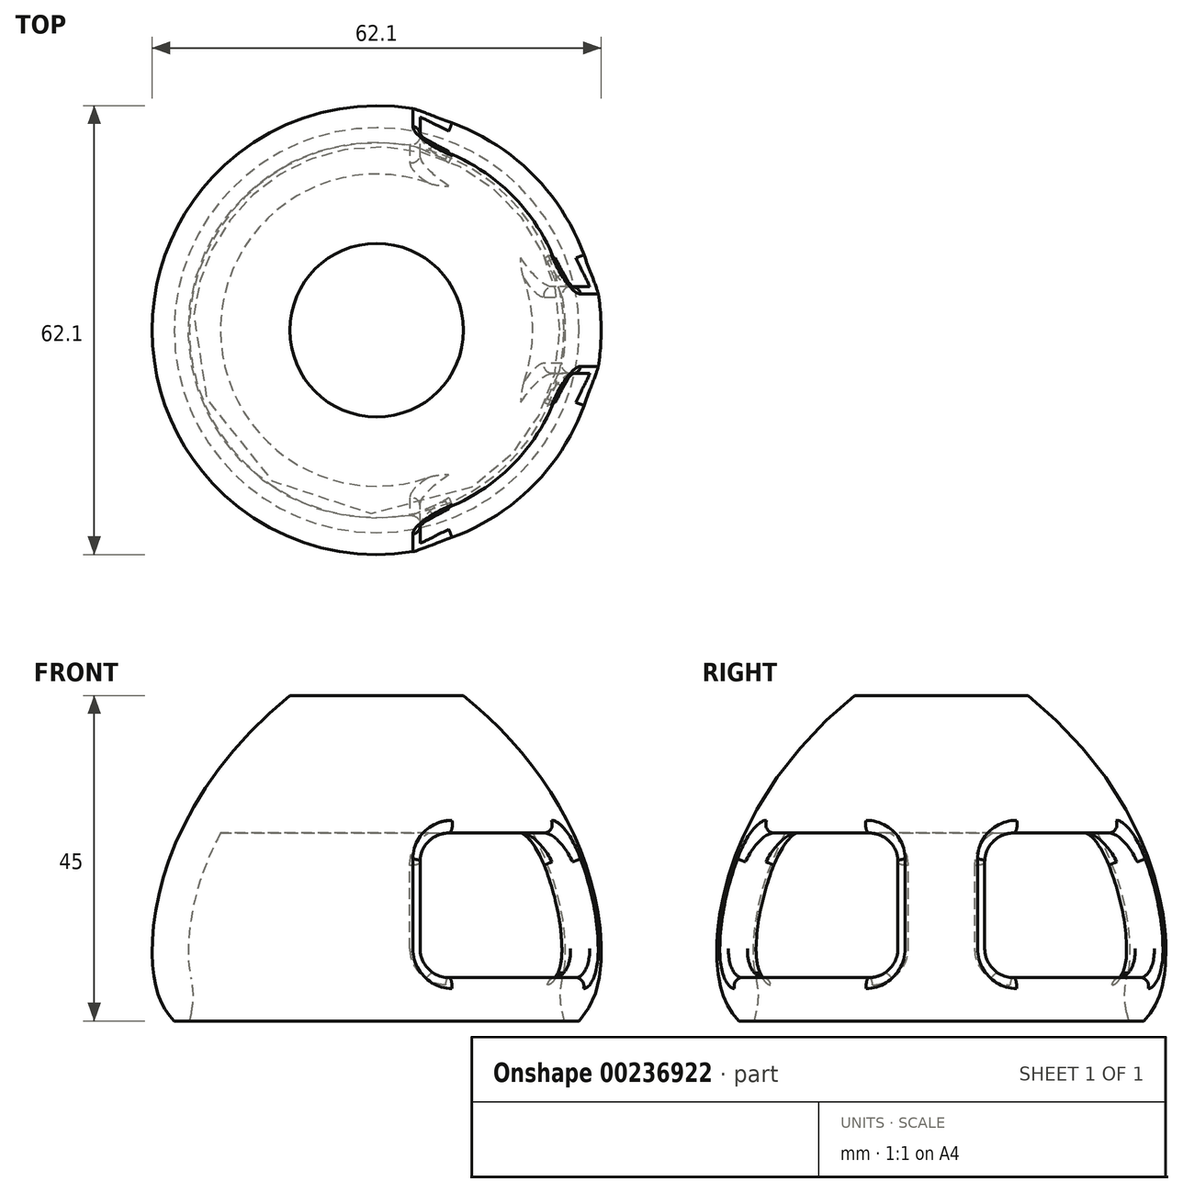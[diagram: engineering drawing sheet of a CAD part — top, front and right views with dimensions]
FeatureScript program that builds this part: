
annotation { "Feature Type Name" : "Feature", "Feature Type Description" : "" }
export const myFeature = defineFeature(function(context is Context, id is Id, definition is map)
    precondition{}
    {
        {
            var Q0;
            Q0=qCreatedBy(makeId("Front.planeOp"),FACE);
            var sketch = newSketch(context, id + "F0", { "sketchPlane" : qUnion([Q0])});
            skLineSegment(sketch, "E0", {"start": v(0, 0) * mm, "end": v(0, 45) * mm});
            skLineSegment(sketch, "E1", {"start": v(0, 45) * mm, "end": v(12, 45) * mm});
            skLineSegment(sketch, "E2", {"start": v(0, 0) * mm, "end": v(28, 0) * mm});
            skLineSegment(sketch, "E3", {"start": v(28, 0) * mm, "end": v(28, 8) * mm, "construction": true});
            skLineSegment(sketch, "E4", {"start": v(28, 8) * mm, "end": v(31, 8) * mm, "construction": true});
            skFitSpline(sketch, "E5", {"points": [v(12, 45) * mm, v(31, 8) * mm, v(28, 0) * mm], "startDerivative": vector(69.76, -56.68) * mm, "endDerivative": vector(-16.2, -16.73) * mm});
            skSolve(sketch);
        }
        {
            var Q0;
            Q0 = qSketchRegion(id + "F0", true);
            var Q1;
            Q1=sQuery(id+"F0.wireOp",EDGE,"E0");
            revolve(context, id + "F1", {"entities" : qUnion([Q0]), "axis" : qUnion([Q1]), "revolveType" : RevolveType.FULL});
        }
        {
            var Q0;
            Q0=makeQuery(id+"F1.opRevolve","SWEPT_FACE",FACE,{"disambiguationData":[OSD([sQuery(id+"F0.wireOp",EDGE,"E2")])]});
            shell(context, id + "F2", {"entities" : qUnion([Q0]), "thickness" : 5 * mm});
        }
        {
            var Q0;
            Q0=qCreatedBy(makeId("Top.planeOp"),FACE);
            cPlane(context, id + "F3", {"entities" : qUnion([Q0]), "cplaneType" : CPlaneType.OFFSET, "offset" : 26 * mm, "width" : 150 * mm, "height" : 150 * mm});
        }
        {
            var Q0;
            Q0=qCreatedBy(id+"F3.planeOp",FACE);
            var sketch = newSketch(context, id + "F4", { "sketchPlane" : qUnion([Q0])});
            skCircle(sketch, "E6", {"center": v(0, 0) * mm, "radius": 27.24 * mm});
            skSolve(sketch);
        }
        {
            var Q0;
            Q0 = qSketchRegion(id + "F4", true);
            var Q1;
            Q1=makeQuery(id+"F1.opRevolve","SWEPT_BODY",BODY,{"disambiguationData":[OSD([sQuery(id+"F0.wireOp",EDGE,"E0"),sQuery(id+"F0.wireOp",EDGE,"E1"),sQuery(id+"F0.wireOp",EDGE,"E2"),sQuery(id+"F0.wireOp",EDGE,"E5")])]});
            extrude(context, id + "F5", {"entities" : qUnion([Q0]), "operationType" : NewBodyOperationType.ADD, "endBound" : BoundingType.UP_TO_BODY, "endBoundEntityBody" : qUnion([Q1]), "depth" : 25 * mm});
        }
        {
            var Q0;
            Q0=makeQuery(id+"F2.opShell","OFFSET_EDGE",EDGE,{"disambiguationData":[OSD([sQuery(id+"F0.wireOp",EDGE,"E2"),sQuery(id+"F0.wireOp",EDGE,"E5")])]});
            chamfer(context, id + "F6", {"entities" : qUnion([Q0]), "chamferType" : ChamferType.TWO_OFFSETS, "width1" : 6 * mm, "oppositeDirection" : false, "width2" : 5 * mm, "tangentPropagation" : true});
        }
        {
            var Q0;
            {var subQ0=sQuery(id+"F0.wireOp",EDGE,"E5");Q0=makeQuery(id+"F6.opChamfer","BLEND_EDGE",EDGE,{"blendedFrom":[makeQuery(id+"F2.opShell","OFFSET_EDGE",EDGE,{"disambiguationData":[OSD([sQuery(id+"F0.wireOp",EDGE,"E2"),subQ0])]}),makeQuery(id+"F2.opShell","OFFSET_FACE",FACE,{"disambiguationData":[OSD([subQ0])]})],"blendedInto":[makeQuery(id+"F2.opShell","OFFSET_FACE",FACE,{"disambiguationData":[OSD([subQ0])]})]});}
            fillet(context, id + "F7", {"entities" : qUnion([Q0]), "radius" : 10 * mm, "tangentPropagation" : true, "allowEdgeOverflow" : false});
        }
        {
            var Q0;
            Q0=qCreatedBy(makeId("Top.planeOp"),FACE);
            cPlane(context, id + "F8", {"entities" : qUnion([Q0]), "cplaneType" : CPlaneType.OFFSET, "offset" : 6 * mm, "width" : 150 * mm, "height" : 150 * mm});
        }
        {
            var Q0;
            Q0=qCreatedBy(id+"F8.planeOp",FACE);
            var sketch = newSketch(context, id + "F9", { "sketchPlane" : qUnion([Q0])});
            skLineSegment(sketch, "E7.bottom", {"start": v(6, -44.78) * mm, "end": v(-6, -44.78) * mm});
            skLineSegment(sketch, "E7.top", {"start": v(6, 44.78) * mm, "end": v(-6, 44.78) * mm});
            skLineSegment(sketch, "E7.left", {"start": v(6, -44.78) * mm, "end": v(6, 44.78) * mm});
            skLineSegment(sketch, "E7.right", {"start": v(-6, -44.78) * mm, "end": v(-6, 44.78) * mm});
            skPoint(sketch, "E7.middle", {"position": v(0, 0) * mm});
            skLineSegment(sketch, "E8.bottom", {"start": v(39.59, 6) * mm, "end": v(-39.59, 6) * mm});
            skLineSegment(sketch, "E8.top", {"start": v(39.59, -6) * mm, "end": v(-39.59, -6) * mm});
            skLineSegment(sketch, "E8.left", {"start": v(39.59, 6) * mm, "end": v(39.59, -6) * mm});
            skLineSegment(sketch, "E8.right", {"start": v(-39.59, 6) * mm, "end": v(-39.59, -6) * mm});
            skCircle(sketch, "E9", {"center": v(0, 0) * mm, "radius": 40.04 * mm});
            skSolve(sketch);
        }
        {
            var Q0;
            {var subQ0=sQuery(id+"F9.wireOp",EDGE,"E9");var subQ1=sQuery(id+"F9.wireOp",EDGE,"E7.right");var subQ2=makeQuery(id+"F9.imprint","INTERSECT",VERTEX,{"disambiguationData":[OD(0.0)],"derivedFrom":[subQ1,subQ0]});Q0=makeQuery(id+"F9.imprint","IMPRINT",FACE,{"disambiguationData":[TD([[makeQuery(id+"F9.imprint","IMPRINT",EDGE,{"disambiguationData":[TD([[subQ2,-1.0]])],"derivedFrom":subQ1}),1.0]])]});}
            var Q1;
            {var subQ0=sQuery(id+"F9.wireOp",EDGE,"E9");var subQ1=sQuery(id+"F9.wireOp",EDGE,"E7.left");var subQ2=makeQuery(id+"F9.imprint","INTERSECT",VERTEX,{"disambiguationData":[OD(0.0)],"derivedFrom":[subQ1,subQ0]});Q1=makeQuery(id+"F9.imprint","IMPRINT",FACE,{"disambiguationData":[TD([[makeQuery(id+"F9.imprint","IMPRINT",EDGE,{"disambiguationData":[TD([[subQ2,-1.0]])],"derivedFrom":subQ1}),-1.0]])]});}
            var Q2;
            {var subQ0=sQuery(id+"F9.wireOp",EDGE,"E9");var subQ1=sQuery(id+"F9.wireOp",EDGE,"E7.right");var subQ2=makeQuery(id+"F9.imprint","INTERSECT",VERTEX,{"disambiguationData":[OD(1.0)],"derivedFrom":[subQ1,subQ0]});Q2=makeQuery(id+"F9.imprint","IMPRINT",FACE,{"disambiguationData":[TD([[makeQuery(id+"F9.imprint","IMPRINT",EDGE,{"disambiguationData":[TD([[subQ2,1.0]])],"derivedFrom":subQ1}),1.0]])]});}
            var Q3;
            {var subQ0=sQuery(id+"F9.wireOp",EDGE,"E9");var subQ1=sQuery(id+"F9.wireOp",EDGE,"E7.left");var subQ2=makeQuery(id+"F9.imprint","INTERSECT",VERTEX,{"disambiguationData":[OD(1.0)],"derivedFrom":[subQ1,subQ0]});Q3=makeQuery(id+"F9.imprint","IMPRINT",FACE,{"disambiguationData":[TD([[makeQuery(id+"F9.imprint","IMPRINT",EDGE,{"disambiguationData":[TD([[subQ2,1.0]])],"derivedFrom":subQ1}),-1.0]])]});}
            var Q4;
            Q4=makeQuery(id+"F5.opExtrude","CAP_FACE",FACE,{"disambiguationData":[OSD([sQuery(id+"F4.wireOp",EDGE,"E6")])],"isStart":true});
            extrude(context, id + "F10", {"entities" : qUnion([Q0, Q1, Q2, Q3]), "operationType" : NewBodyOperationType.REMOVE, "endBound" : BoundingType.UP_TO_SURFACE, "endBoundEntityFace" : qUnion([Q4]), "depth" : 25 * mm});
        }
        {
            var Q0;
            {var subQ0=sQuery(id+"F9.wireOp",EDGE,"E7.right");Q0=makeQuery(id+"F10.boolean.opBoolean","COPY",EDGE,{"derivedFrom":makeQuery(id+"F10.opExtrude","CAP_EDGE",EDGE,{"disambiguationData":[OSD([subQ0]),TDD([makeQuery(id+"F9.imprint","IMPRINT",EDGE,{"disambiguationData":[TD([[makeQuery(id+"F9.imprint","INTERSECT",VERTEX,{"disambiguationData":[OD(0.0)],"derivedFrom":[subQ0,sQuery(id+"F9.wireOp",EDGE,"E9")]}),-1.0]])],"derivedFrom":subQ0})])],"isStart":true})});}
            var Q1;
            {var subQ0=sQuery(id+"F9.wireOp",EDGE,"E7.right");Q1=makeQuery(id+"F10.boolean.opBoolean","COPY",EDGE,{"derivedFrom":makeQuery(id+"F10.opExtrude","CAP_EDGE",EDGE,{"disambiguationData":[OSD([subQ0]),TDD([makeQuery(id+"F9.imprint","IMPRINT",EDGE,{"disambiguationData":[TD([[makeQuery(id+"F9.imprint","INTERSECT",VERTEX,{"disambiguationData":[OD(0.0)],"derivedFrom":[subQ0,sQuery(id+"F9.wireOp",EDGE,"E9")]}),-1.0]])],"derivedFrom":subQ0})])],"isStart":false})});}
            var Q2;
            {var subQ0=sQuery(id+"F9.wireOp",EDGE,"E8.top");Q2=makeQuery(id+"F10.boolean.opBoolean","COPY",EDGE,{"derivedFrom":makeQuery(id+"F10.opExtrude","CAP_EDGE",EDGE,{"disambiguationData":[OSD([subQ0]),TDD([makeQuery(id+"F9.imprint","IMPRINT",EDGE,{"disambiguationData":[TD([[makeQuery(id+"F9.imprint","INTERSECT",VERTEX,{"derivedFrom":[sQuery(id+"F9.wireOp",EDGE,"E7.right"),subQ0]}),-1.0]])],"derivedFrom":subQ0})])],"isStart":false})});}
            var Q3;
            {var subQ0=sQuery(id+"F9.wireOp",EDGE,"E8.top");Q3=makeQuery(id+"F10.boolean.opBoolean","COPY",EDGE,{"derivedFrom":makeQuery(id+"F10.opExtrude","CAP_EDGE",EDGE,{"disambiguationData":[OSD([subQ0]),TDD([makeQuery(id+"F9.imprint","IMPRINT",EDGE,{"disambiguationData":[TD([[makeQuery(id+"F9.imprint","INTERSECT",VERTEX,{"derivedFrom":[sQuery(id+"F9.wireOp",EDGE,"E7.right"),subQ0]}),-1.0]])],"derivedFrom":subQ0})])],"isStart":true})});}
            var Q4;
            {var subQ0=sQuery(id+"F9.wireOp",EDGE,"E8.bottom");Q4=makeQuery(id+"F10.boolean.opBoolean","COPY",EDGE,{"derivedFrom":makeQuery(id+"F10.opExtrude","CAP_EDGE",EDGE,{"disambiguationData":[OSD([subQ0]),TDD([makeQuery(id+"F9.imprint","IMPRINT",EDGE,{"disambiguationData":[TD([[makeQuery(id+"F9.imprint","INTERSECT",VERTEX,{"derivedFrom":[sQuery(id+"F9.wireOp",EDGE,"E7.right"),subQ0]}),-1.0]])],"derivedFrom":subQ0})])],"isStart":true})});}
            var Q5;
            {var subQ0=sQuery(id+"F9.wireOp",EDGE,"E8.bottom");Q5=makeQuery(id+"F10.boolean.opBoolean","COPY",EDGE,{"derivedFrom":makeQuery(id+"F10.opExtrude","CAP_EDGE",EDGE,{"disambiguationData":[OSD([subQ0]),TDD([makeQuery(id+"F9.imprint","IMPRINT",EDGE,{"disambiguationData":[TD([[makeQuery(id+"F9.imprint","INTERSECT",VERTEX,{"derivedFrom":[sQuery(id+"F9.wireOp",EDGE,"E7.right"),subQ0]}),-1.0]])],"derivedFrom":subQ0})])],"isStart":false})});}
            var Q6;
            {var subQ0=sQuery(id+"F9.wireOp",EDGE,"E7.right");Q6=makeQuery(id+"F10.boolean.opBoolean","COPY",EDGE,{"derivedFrom":makeQuery(id+"F10.opExtrude","CAP_EDGE",EDGE,{"disambiguationData":[OSD([subQ0]),TDD([makeQuery(id+"F9.imprint","IMPRINT",EDGE,{"disambiguationData":[TD([[makeQuery(id+"F9.imprint","INTERSECT",VERTEX,{"disambiguationData":[OD(1.0)],"derivedFrom":[subQ0,sQuery(id+"F9.wireOp",EDGE,"E9")]}),1.0]])],"derivedFrom":subQ0})])],"isStart":false})});}
            var Q7;
            {var subQ0=sQuery(id+"F9.wireOp",EDGE,"E7.right");Q7=makeQuery(id+"F10.boolean.opBoolean","COPY",EDGE,{"derivedFrom":makeQuery(id+"F10.opExtrude","CAP_EDGE",EDGE,{"disambiguationData":[OSD([subQ0]),TDD([makeQuery(id+"F9.imprint","IMPRINT",EDGE,{"disambiguationData":[TD([[makeQuery(id+"F9.imprint","INTERSECT",VERTEX,{"disambiguationData":[OD(1.0)],"derivedFrom":[subQ0,sQuery(id+"F9.wireOp",EDGE,"E9")]}),1.0]])],"derivedFrom":subQ0})])],"isStart":true})});}
            var Q8;
            {var subQ0=sQuery(id+"F9.wireOp",EDGE,"E7.left");Q8=makeQuery(id+"F10.boolean.opBoolean","COPY",EDGE,{"derivedFrom":makeQuery(id+"F10.opExtrude","CAP_EDGE",EDGE,{"disambiguationData":[OSD([subQ0]),TDD([makeQuery(id+"F9.imprint","IMPRINT",EDGE,{"disambiguationData":[TD([[makeQuery(id+"F9.imprint","INTERSECT",VERTEX,{"disambiguationData":[OD(1.0)],"derivedFrom":[subQ0,sQuery(id+"F9.wireOp",EDGE,"E9")]}),1.0]])],"derivedFrom":subQ0})])],"isStart":true})});}
            var Q9;
            {var subQ0=sQuery(id+"F9.wireOp",EDGE,"E7.left");Q9=makeQuery(id+"F10.boolean.opBoolean","COPY",EDGE,{"derivedFrom":makeQuery(id+"F10.opExtrude","CAP_EDGE",EDGE,{"disambiguationData":[OSD([subQ0]),TDD([makeQuery(id+"F9.imprint","IMPRINT",EDGE,{"disambiguationData":[TD([[makeQuery(id+"F9.imprint","INTERSECT",VERTEX,{"disambiguationData":[OD(1.0)],"derivedFrom":[subQ0,sQuery(id+"F9.wireOp",EDGE,"E9")]}),1.0]])],"derivedFrom":subQ0})])],"isStart":false})});}
            var Q10;
            {var subQ0=sQuery(id+"F9.wireOp",EDGE,"E8.bottom");Q10=makeQuery(id+"F10.boolean.opBoolean","COPY",EDGE,{"derivedFrom":makeQuery(id+"F10.opExtrude","CAP_EDGE",EDGE,{"disambiguationData":[OSD([subQ0]),TDD([makeQuery(id+"F9.imprint","IMPRINT",EDGE,{"disambiguationData":[TD([[makeQuery(id+"F9.imprint","INTERSECT",VERTEX,{"derivedFrom":[sQuery(id+"F9.wireOp",EDGE,"E7.left"),subQ0]}),1.0]])],"derivedFrom":subQ0})])],"isStart":false})});}
            var Q11;
            {var subQ0=sQuery(id+"F9.wireOp",EDGE,"E8.bottom");Q11=makeQuery(id+"F10.boolean.opBoolean","COPY",EDGE,{"derivedFrom":makeQuery(id+"F10.opExtrude","CAP_EDGE",EDGE,{"disambiguationData":[OSD([subQ0]),TDD([makeQuery(id+"F9.imprint","IMPRINT",EDGE,{"disambiguationData":[TD([[makeQuery(id+"F9.imprint","INTERSECT",VERTEX,{"derivedFrom":[sQuery(id+"F9.wireOp",EDGE,"E7.left"),subQ0]}),1.0]])],"derivedFrom":subQ0})])],"isStart":true})});}
            var Q12;
            {var subQ0=sQuery(id+"F9.wireOp",EDGE,"E8.top");Q12=makeQuery(id+"F10.boolean.opBoolean","COPY",EDGE,{"derivedFrom":makeQuery(id+"F10.opExtrude","CAP_EDGE",EDGE,{"disambiguationData":[OSD([subQ0]),TDD([makeQuery(id+"F9.imprint","IMPRINT",EDGE,{"disambiguationData":[TD([[makeQuery(id+"F9.imprint","INTERSECT",VERTEX,{"derivedFrom":[sQuery(id+"F9.wireOp",EDGE,"E7.left"),subQ0]}),1.0]])],"derivedFrom":subQ0})])],"isStart":true})});}
            var Q13;
            {var subQ0=sQuery(id+"F9.wireOp",EDGE,"E7.left");Q13=makeQuery(id+"F10.boolean.opBoolean","COPY",EDGE,{"derivedFrom":makeQuery(id+"F10.opExtrude","CAP_EDGE",EDGE,{"disambiguationData":[OSD([subQ0]),TDD([makeQuery(id+"F9.imprint","IMPRINT",EDGE,{"disambiguationData":[TD([[makeQuery(id+"F9.imprint","INTERSECT",VERTEX,{"disambiguationData":[OD(0.0)],"derivedFrom":[subQ0,sQuery(id+"F9.wireOp",EDGE,"E9")]}),-1.0]])],"derivedFrom":subQ0})])],"isStart":true})});}
            var Q14;
            {var subQ0=sQuery(id+"F9.wireOp",EDGE,"E7.left");Q14=makeQuery(id+"F10.boolean.opBoolean","COPY",EDGE,{"derivedFrom":makeQuery(id+"F10.opExtrude","CAP_EDGE",EDGE,{"disambiguationData":[OSD([subQ0]),TDD([makeQuery(id+"F9.imprint","IMPRINT",EDGE,{"disambiguationData":[TD([[makeQuery(id+"F9.imprint","INTERSECT",VERTEX,{"disambiguationData":[OD(0.0)],"derivedFrom":[subQ0,sQuery(id+"F9.wireOp",EDGE,"E9")]}),-1.0]])],"derivedFrom":subQ0})])],"isStart":false})});}
            var Q15;
            {var subQ0=sQuery(id+"F9.wireOp",EDGE,"E8.top");Q15=makeQuery(id+"F10.boolean.opBoolean","COPY",EDGE,{"derivedFrom":makeQuery(id+"F10.opExtrude","CAP_EDGE",EDGE,{"disambiguationData":[OSD([subQ0]),TDD([makeQuery(id+"F9.imprint","IMPRINT",EDGE,{"disambiguationData":[TD([[makeQuery(id+"F9.imprint","INTERSECT",VERTEX,{"derivedFrom":[sQuery(id+"F9.wireOp",EDGE,"E7.left"),subQ0]}),1.0]])],"derivedFrom":subQ0})])],"isStart":false})});}
            fillet(context, id + "F11", {"entities" : qUnion([Q0, Q1, Q2, Q3, Q4, Q5, Q6, Q7, Q8, Q9, Q10, Q11, Q12, Q13, Q14, Q15]), "radius" : 4 * mm, "tangentPropagation" : true, "allowEdgeOverflow" : false});
        }
        {
            var Q0;
            {var subQ0=sQuery(id+"F9.wireOp",EDGE,"E9");var subQ1=sQuery(id+"F9.wireOp",EDGE,"E8.bottom");var subQ2=sQuery(id+"F9.wireOp",EDGE,"E7.right");var subQ3=makeQuery(id+"F1.opRevolve","SWEPT_FACE",FACE,{"disambiguationData":[OSD([sQuery(id+"F0.wireOp",EDGE,"E5")])]});var subQ4=sQuery(id+"F9.wireOp",EDGE,"E8.top");var subQ5=sQuery(id+"F9.wireOp",EDGE,"E7.left");Q0=qUnion([makeQuery(id+"F10.boolean.opBoolean","INTERSECT",EDGE,{"derivedFrom":[subQ3,makeQuery(id+"F10.opExtrude","CAP_FACE",FACE,{"disambiguationData":[OSD([subQ2,subQ4,subQ0])],"isStart":false})]}),makeQuery(id+"F10.boolean.opBoolean","INTERSECT",EDGE,{"derivedFrom":[subQ3,makeQuery(id+"F10.opExtrude","CAP_FACE",FACE,{"disambiguationData":[OSD([subQ5,subQ1,subQ0])],"isStart":false})]}),makeQuery(id+"F10.boolean.opBoolean","INTERSECT",EDGE,{"derivedFrom":[subQ3,makeQuery(id+"F10.opExtrude","CAP_FACE",FACE,{"disambiguationData":[OSD([subQ5,subQ4,subQ0])],"isStart":false})]}),makeQuery(id+"F10.boolean.opBoolean","INTERSECT",EDGE,{"derivedFrom":[subQ3,makeQuery(id+"F10.opExtrude","CAP_FACE",FACE,{"disambiguationData":[OSD([subQ2,subQ1,subQ0])],"isStart":false})]})]);}
            var Q1;
            {var subQ0=sQuery(id+"F9.wireOp",EDGE,"E9");var subQ1=sQuery(id+"F9.wireOp",EDGE,"E8.bottom");var subQ2=sQuery(id+"F9.wireOp",EDGE,"E7.right");var subQ3=makeQuery(id+"F1.opRevolve","SWEPT_FACE",FACE,{"disambiguationData":[OSD([sQuery(id+"F0.wireOp",EDGE,"E5")])]});var subQ4=sQuery(id+"F9.wireOp",EDGE,"E8.top");var subQ5=sQuery(id+"F9.wireOp",EDGE,"E7.left");Q1=qUnion([makeQuery(id+"F10.boolean.opBoolean","INTERSECT",EDGE,{"derivedFrom":[subQ3,makeQuery(id+"F10.opExtrude","CAP_FACE",FACE,{"disambiguationData":[OSD([subQ2,subQ4,subQ0])],"isStart":false})]}),makeQuery(id+"F10.boolean.opBoolean","INTERSECT",EDGE,{"derivedFrom":[subQ3,makeQuery(id+"F10.opExtrude","CAP_FACE",FACE,{"disambiguationData":[OSD([subQ5,subQ1,subQ0])],"isStart":false})]}),makeQuery(id+"F10.boolean.opBoolean","INTERSECT",EDGE,{"derivedFrom":[subQ3,makeQuery(id+"F10.opExtrude","CAP_FACE",FACE,{"disambiguationData":[OSD([subQ5,subQ4,subQ0])],"isStart":false})]}),makeQuery(id+"F10.boolean.opBoolean","INTERSECT",EDGE,{"derivedFrom":[subQ3,makeQuery(id+"F10.opExtrude","CAP_FACE",FACE,{"disambiguationData":[OSD([subQ2,subQ1,subQ0])],"isStart":false})]})]);}
            var Q2;
            {var subQ0=sQuery(id+"F9.wireOp",EDGE,"E9");var subQ1=sQuery(id+"F9.wireOp",EDGE,"E8.bottom");var subQ2=sQuery(id+"F9.wireOp",EDGE,"E7.right");var subQ3=makeQuery(id+"F1.opRevolve","SWEPT_FACE",FACE,{"disambiguationData":[OSD([sQuery(id+"F0.wireOp",EDGE,"E5")])]});var subQ4=sQuery(id+"F9.wireOp",EDGE,"E8.top");var subQ5=sQuery(id+"F9.wireOp",EDGE,"E7.left");Q2=qUnion([makeQuery(id+"F10.boolean.opBoolean","INTERSECT",EDGE,{"derivedFrom":[subQ3,makeQuery(id+"F10.opExtrude","CAP_FACE",FACE,{"disambiguationData":[OSD([subQ2,subQ4,subQ0])],"isStart":false})]}),makeQuery(id+"F10.boolean.opBoolean","INTERSECT",EDGE,{"derivedFrom":[subQ3,makeQuery(id+"F10.opExtrude","CAP_FACE",FACE,{"disambiguationData":[OSD([subQ5,subQ1,subQ0])],"isStart":false})]}),makeQuery(id+"F10.boolean.opBoolean","INTERSECT",EDGE,{"derivedFrom":[subQ3,makeQuery(id+"F10.opExtrude","CAP_FACE",FACE,{"disambiguationData":[OSD([subQ5,subQ4,subQ0])],"isStart":false})]}),makeQuery(id+"F10.boolean.opBoolean","INTERSECT",EDGE,{"derivedFrom":[subQ3,makeQuery(id+"F10.opExtrude","CAP_FACE",FACE,{"disambiguationData":[OSD([subQ2,subQ1,subQ0])],"isStart":false})]})]);}
            var Q3;
            {var subQ0=sQuery(id+"F9.wireOp",EDGE,"E9");var subQ1=sQuery(id+"F9.wireOp",EDGE,"E8.bottom");var subQ2=sQuery(id+"F9.wireOp",EDGE,"E7.right");var subQ3=makeQuery(id+"F1.opRevolve","SWEPT_FACE",FACE,{"disambiguationData":[OSD([sQuery(id+"F0.wireOp",EDGE,"E5")])]});var subQ4=sQuery(id+"F9.wireOp",EDGE,"E8.top");var subQ5=sQuery(id+"F9.wireOp",EDGE,"E7.left");Q3=qUnion([makeQuery(id+"F10.boolean.opBoolean","INTERSECT",EDGE,{"derivedFrom":[subQ3,makeQuery(id+"F10.opExtrude","CAP_FACE",FACE,{"disambiguationData":[OSD([subQ2,subQ4,subQ0])],"isStart":false})]}),makeQuery(id+"F10.boolean.opBoolean","INTERSECT",EDGE,{"derivedFrom":[subQ3,makeQuery(id+"F10.opExtrude","CAP_FACE",FACE,{"disambiguationData":[OSD([subQ5,subQ1,subQ0])],"isStart":false})]}),makeQuery(id+"F10.boolean.opBoolean","INTERSECT",EDGE,{"derivedFrom":[subQ3,makeQuery(id+"F10.opExtrude","CAP_FACE",FACE,{"disambiguationData":[OSD([subQ5,subQ4,subQ0])],"isStart":false})]}),makeQuery(id+"F10.boolean.opBoolean","INTERSECT",EDGE,{"derivedFrom":[subQ3,makeQuery(id+"F10.opExtrude","CAP_FACE",FACE,{"disambiguationData":[OSD([subQ2,subQ1,subQ0])],"isStart":false})]})]);}
            var Q4;
            {var subQ0=sQuery(id+"F9.wireOp",EDGE,"E8.top");Q4=makeQuery(id+"F10.boolean.opBoolean","INTERSECT",EDGE,{"derivedFrom":[makeQuery(id+"F2.opShell","OFFSET_FACE",FACE,{"disambiguationData":[OSD([sQuery(id+"F0.wireOp",EDGE,"E5")])]}),makeQuery(id+"F10.opExtrude","SWEPT_FACE",FACE,{"disambiguationData":[OSD([subQ0]),TDD([makeQuery(id+"F9.imprint","IMPRINT",EDGE,{"disambiguationData":[TD([[makeQuery(id+"F9.imprint","INTERSECT",VERTEX,{"derivedFrom":[sQuery(id+"F9.wireOp",EDGE,"E7.right"),subQ0]}),-1.0]])],"derivedFrom":subQ0})])]})]});}
            var Q5;
            {var subQ0=sQuery(id+"F9.wireOp",EDGE,"E7.right");Q5=makeQuery(id+"F10.boolean.opBoolean","INTERSECT",EDGE,{"derivedFrom":[makeQuery(id+"F2.opShell","OFFSET_FACE",FACE,{"disambiguationData":[OSD([sQuery(id+"F0.wireOp",EDGE,"E5")])]}),makeQuery(id+"F10.opExtrude","SWEPT_FACE",FACE,{"disambiguationData":[OSD([subQ0]),TDD([makeQuery(id+"F9.imprint","IMPRINT",EDGE,{"disambiguationData":[TD([[makeQuery(id+"F9.imprint","INTERSECT",VERTEX,{"disambiguationData":[OD(1.0)],"derivedFrom":[subQ0,sQuery(id+"F9.wireOp",EDGE,"E9")]}),1.0]])],"derivedFrom":subQ0})])]})]});}
            var Q6;
            {var subQ0=sQuery(id+"F9.wireOp",EDGE,"E7.left");Q6=makeQuery(id+"F10.boolean.opBoolean","INTERSECT",EDGE,{"derivedFrom":[makeQuery(id+"F2.opShell","OFFSET_FACE",FACE,{"disambiguationData":[OSD([sQuery(id+"F0.wireOp",EDGE,"E5")])]}),makeQuery(id+"F10.opExtrude","SWEPT_FACE",FACE,{"disambiguationData":[OSD([subQ0]),TDD([makeQuery(id+"F9.imprint","IMPRINT",EDGE,{"disambiguationData":[TD([[makeQuery(id+"F9.imprint","INTERSECT",VERTEX,{"disambiguationData":[OD(1.0)],"derivedFrom":[subQ0,sQuery(id+"F9.wireOp",EDGE,"E9")]}),1.0]])],"derivedFrom":subQ0})])]})]});}
            var Q7;
            {var subQ0=sQuery(id+"F9.wireOp",EDGE,"E8.top");Q7=makeQuery(id+"F10.boolean.opBoolean","INTERSECT",EDGE,{"derivedFrom":[makeQuery(id+"F2.opShell","OFFSET_FACE",FACE,{"disambiguationData":[OSD([sQuery(id+"F0.wireOp",EDGE,"E5")])]}),makeQuery(id+"F10.opExtrude","SWEPT_FACE",FACE,{"disambiguationData":[OSD([subQ0]),TDD([makeQuery(id+"F9.imprint","IMPRINT",EDGE,{"disambiguationData":[TD([[makeQuery(id+"F9.imprint","INTERSECT",VERTEX,{"derivedFrom":[sQuery(id+"F9.wireOp",EDGE,"E7.left"),subQ0]}),1.0]])],"derivedFrom":subQ0})])]})]});}
            var Q8;
            {var subQ0=sQuery(id+"F9.wireOp",EDGE,"E8.bottom");Q8=makeQuery(id+"F10.boolean.opBoolean","INTERSECT",EDGE,{"derivedFrom":[makeQuery(id+"F2.opShell","OFFSET_FACE",FACE,{"disambiguationData":[OSD([sQuery(id+"F0.wireOp",EDGE,"E5")])]}),makeQuery(id+"F10.opExtrude","SWEPT_FACE",FACE,{"disambiguationData":[OSD([subQ0]),TDD([makeQuery(id+"F9.imprint","IMPRINT",EDGE,{"disambiguationData":[TD([[makeQuery(id+"F9.imprint","INTERSECT",VERTEX,{"derivedFrom":[sQuery(id+"F9.wireOp",EDGE,"E7.left"),subQ0]}),1.0]])],"derivedFrom":subQ0})])]})]});}
            var Q9;
            {var subQ0=sQuery(id+"F9.wireOp",EDGE,"E7.right");Q9=makeQuery(id+"F10.boolean.opBoolean","INTERSECT",EDGE,{"derivedFrom":[makeQuery(id+"F2.opShell","OFFSET_FACE",FACE,{"disambiguationData":[OSD([sQuery(id+"F0.wireOp",EDGE,"E5")])]}),makeQuery(id+"F10.opExtrude","SWEPT_FACE",FACE,{"disambiguationData":[OSD([subQ0]),TDD([makeQuery(id+"F9.imprint","IMPRINT",EDGE,{"disambiguationData":[TD([[makeQuery(id+"F9.imprint","INTERSECT",VERTEX,{"disambiguationData":[OD(0.0)],"derivedFrom":[subQ0,sQuery(id+"F9.wireOp",EDGE,"E9")]}),-1.0]])],"derivedFrom":subQ0})])]})]});}
            fillet(context, id + "F12", {"entities" : qUnion([Q0, Q1, Q2, Q3, Q4, Q5, Q6, Q7, Q8, Q9]), "radius" : 1.2 * mm, "tangentPropagation" : true, "allowEdgeOverflow" : false});
        }
    });
